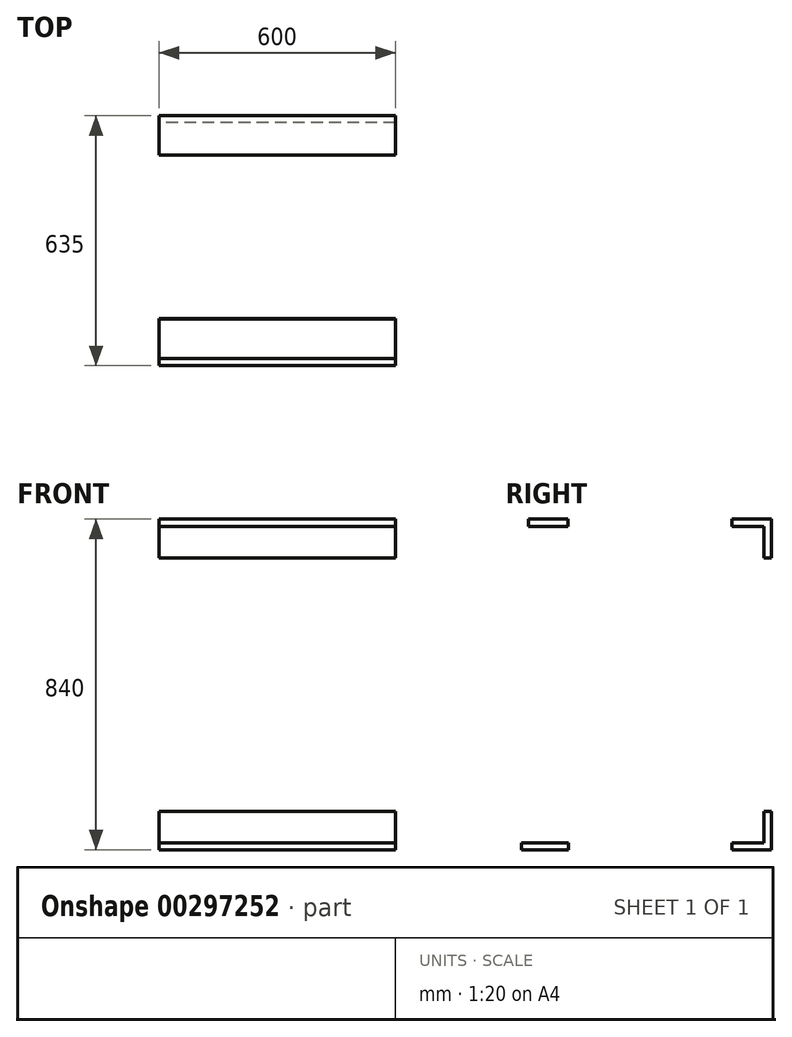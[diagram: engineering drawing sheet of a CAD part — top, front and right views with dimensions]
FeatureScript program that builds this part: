
annotation { "Feature Type Name" : "Feature", "Feature Type Description" : "" }
export const myFeature = defineFeature(function(context is Context, id is Id, definition is map)
    precondition{}
    {
        {
            var Q0;
            Q0=qCreatedBy(makeId("Right.planeOp"),FACE);
            var sketch = newSketch(context, id + "F0", { "sketchPlane" : qUnion([Q0])});
            skLineSegment(sketch, "E0.bottom", {"start": v(317.5, 420) * mm, "end": v(-317.5, 420) * mm, "construction": true});
            skLineSegment(sketch, "E0.top", {"start": v(317.5, -420) * mm, "end": v(-317.5, -420) * mm, "construction": true});
            skLineSegment(sketch, "E0.left", {"start": v(317.5, 420) * mm, "end": v(317.5, -420) * mm, "construction": true});
            skLineSegment(sketch, "E0.right", {"start": v(-317.5, 420) * mm, "end": v(-317.5, -420) * mm, "construction": true});
            skPoint(sketch, "E0.middle", {"position": v(0, 0) * mm});
            skLineSegment(sketch, "E1.bottom", {"start": v(317.5, 420) * mm, "end": v(217.5, 420) * mm});
            skLineSegment(sketch, "E1.top", {"start": v(317.5, 402) * mm, "end": v(217.5, 402) * mm});
            skLineSegment(sketch, "E1.left", {"start": v(317.5, 420) * mm, "end": v(317.5, 402) * mm});
            skLineSegment(sketch, "E1.right", {"start": v(217.5, 420) * mm, "end": v(217.5, 402) * mm});
            skLineSegment(sketch, "E2.bottom", {"start": v(317.5, 402) * mm, "end": v(299.5, 402) * mm});
            skLineSegment(sketch, "E2.top", {"start": v(317.5, 322) * mm, "end": v(299.5, 322) * mm});
            skLineSegment(sketch, "E2.left", {"start": v(317.5, 402) * mm, "end": v(317.5, 322) * mm});
            skLineSegment(sketch, "E2.right", {"start": v(299.5, 402) * mm, "end": v(299.5, 322) * mm});
            skLineSegment(sketch, "E3.bottom", {"start": v(-299.5, 420) * mm, "end": v(-199.5, 420) * mm});
            skLineSegment(sketch, "E3.top", {"start": v(-299.5, 402) * mm, "end": v(-199.5, 402) * mm});
            skLineSegment(sketch, "E3.left", {"start": v(-299.5, 420) * mm, "end": v(-299.5, 402) * mm});
            skLineSegment(sketch, "E3.right", {"start": v(-199.5, 420) * mm, "end": v(-199.5, 402) * mm});
            skLineSegment(sketch, "E4.bottom", {"start": v(-317.5, -420) * mm, "end": v(-197.5, -420) * mm});
            skLineSegment(sketch, "E4.top", {"start": v(-317.5, -402) * mm, "end": v(-197.5, -402) * mm});
            skLineSegment(sketch, "E4.left", {"start": v(-317.5, -420) * mm, "end": v(-317.5, -402) * mm});
            skLineSegment(sketch, "E4.right", {"start": v(-197.5, -420) * mm, "end": v(-197.5, -402) * mm});
            skLineSegment(sketch, "E5.bottom", {"start": v(317.5, -420) * mm, "end": v(217.5, -420) * mm});
            skLineSegment(sketch, "E5.top", {"start": v(317.5, -402) * mm, "end": v(217.5, -402) * mm});
            skLineSegment(sketch, "E5.left", {"start": v(317.5, -420) * mm, "end": v(317.5, -402) * mm});
            skLineSegment(sketch, "E5.right", {"start": v(217.5, -420) * mm, "end": v(217.5, -402) * mm});
            skLineSegment(sketch, "E6.bottom", {"start": v(317.5, -402) * mm, "end": v(299.5, -402) * mm});
            skLineSegment(sketch, "E6.top", {"start": v(317.5, -322) * mm, "end": v(299.5, -322) * mm});
            skLineSegment(sketch, "E6.left", {"start": v(317.5, -402) * mm, "end": v(317.5, -322) * mm});
            skLineSegment(sketch, "E6.right", {"start": v(299.5, -402) * mm, "end": v(299.5, -322) * mm});
            skSolve(sketch);
        }
        {
            var Q0;
            Q0=qSketchRegion(id+"F0",true);
            extrude(context, id + "F1", {"entities" : qUnion([Q0]), "depth" : 600 * mm});
        }
    });
